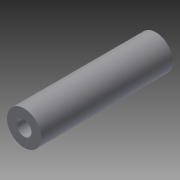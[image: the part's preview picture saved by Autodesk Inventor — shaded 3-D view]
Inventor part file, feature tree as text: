
AUTODESK INVENTOR PART (.ipt)
format: ipt  version: 2015 (Build 190159000, 159)  size: 68,096 bytes
history: native  units: in
note: dims shown in document units (in); Inventor stores cm internally (conversion verified against a paired STEP export)
features: plane x3, sketch x1, extrude x1, reference x1
ambient origin geometry x8: Origin, YZ Plane, XZ Plane, XY Plane, X Axis, Y Axis, Z Axis, Center Point
bodies: Solid1 (feature_tree)
feature tree (6):
  sketch  "Sketch1"  dims[d0=1.0in d1=0.0in]
  plane  "Work Plane1"
  plane  "Work Plane2"
  plane  "Work Plane3"
  extrude  "Extrusion1"  [1 undecoded]
  reference  "Reference2"
note: 1 required parameter value undecoded (feature->parameter linkage not recoverable at this tier; creation-order binding heuristic only, values carry confidence <= 0.55)
